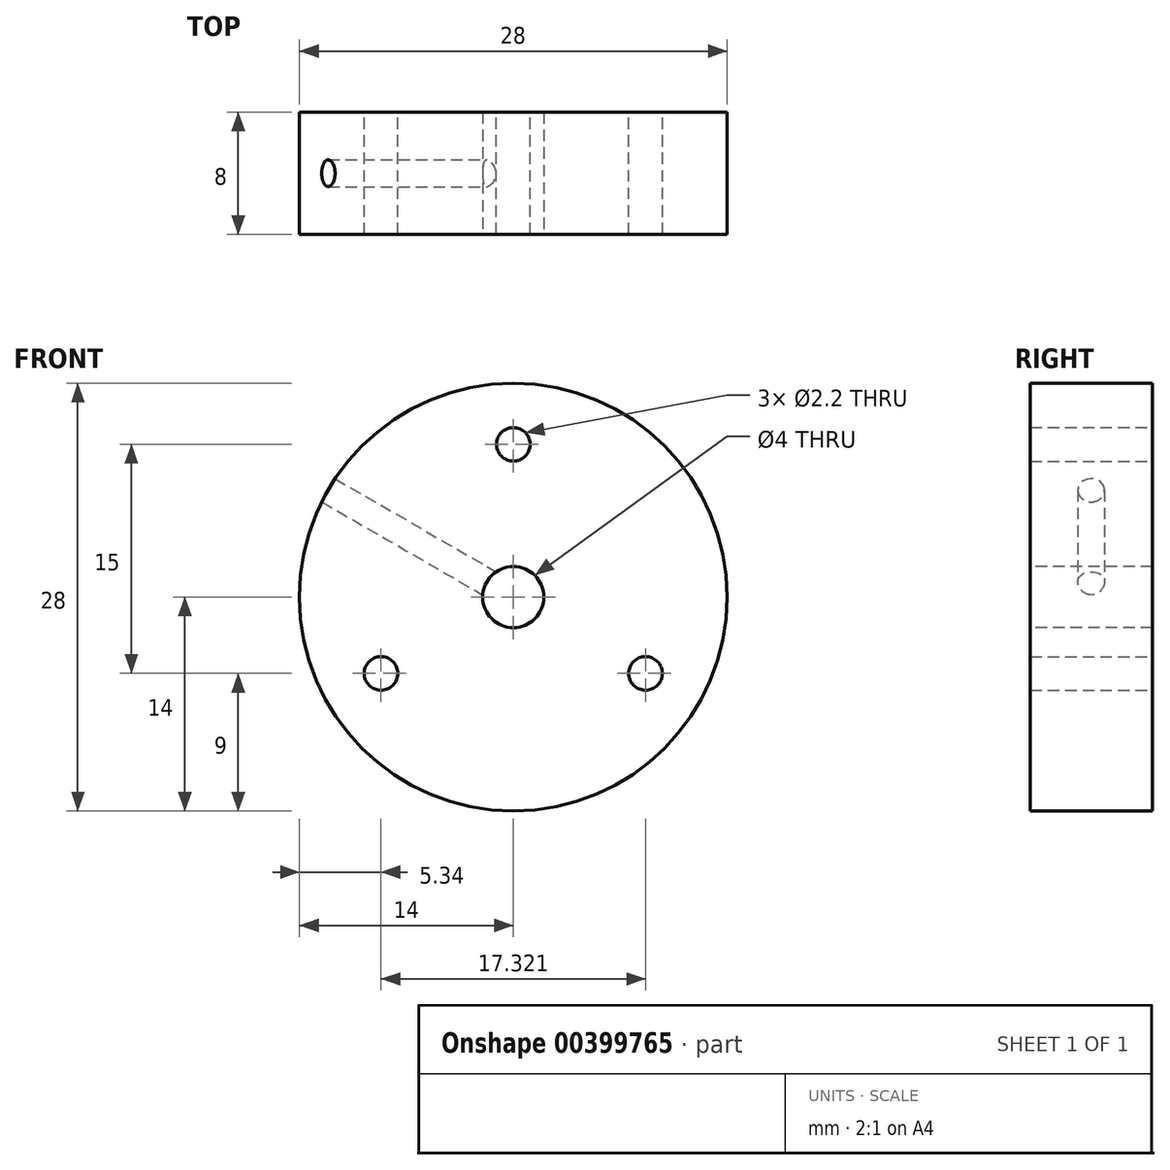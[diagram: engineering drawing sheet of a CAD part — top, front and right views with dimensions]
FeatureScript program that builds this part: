
annotation { "Feature Type Name" : "Feature", "Feature Type Description" : "" }
export const myFeature = defineFeature(function(context is Context, id is Id, definition is map)
    precondition{}
    {
        {
            var Q0;
            Q0=qCreatedBy(makeId("Front.planeOp"),FACE);
            var sketch = newSketch(context, id + "F0", { "sketchPlane" : qUnion([Q0])});
            skCircle(sketch, "E0", {"center": v(0, 0) * mm, "radius": 10 * mm, "construction": true});
            skLineSegment(sketch, "E1.0", {"start": v(0, 10) * mm, "end": v(8.66, -5) * mm, "construction": true});
            skLineSegment(sketch, "E1.1", {"start": v(8.66, -5) * mm, "end": v(-8.66, -5) * mm, "construction": true});
            skLineSegment(sketch, "E1.2", {"start": v(-8.66, -5) * mm, "end": v(0, 10) * mm, "construction": true});
            skCircle(sketch, "E2", {"center": v(0, 10) * mm, "radius": 1.1 * mm});
            skCircle(sketch, "E3", {"center": v(8.66, -5) * mm, "radius": 1.1 * mm});
            skCircle(sketch, "E4", {"center": v(-8.66, -5) * mm, "radius": 1.1 * mm});
            skCircle(sketch, "E5", {"center": v(0, 0) * mm, "radius": 14 * mm});
            skSolve(sketch);
        }
        {
            var Q0;
            Q0=makeQuery(id+"F0.imprint","IMPRINT",FACE,{"disambiguationData":[TD([[makeQuery(id+"F0.imprint","IMPRINT",EDGE,{"derivedFrom":sQuery(id+"F0.wireOp",EDGE,"E2")}),-1.0]])]});
            extrude(context, id + "F1", {"entities" : qUnion([Q0]), "depth" : 8 * mm});
        }
        {
            var Q0;
            Q0=makeQuery(id+"F1.opExtrude","CAP_FACE",FACE,{"disambiguationData":[OSD([sQuery(id+"F0.wireOp",EDGE,"E2"),sQuery(id+"F0.wireOp",EDGE,"E3"),sQuery(id+"F0.wireOp",EDGE,"E4"),sQuery(id+"F0.wireOp",EDGE,"E5")])],"isStart":false});
            var sketch = newSketch(context, id + "F2", { "sketchPlane" : qUnion([Q0])});
            skCircle(sketch, "E6", {"center": v(0, 0) * mm, "radius": 2 * mm});
            skSolve(sketch);
        }
        {
            var Q0;
            Q0 = qSketchRegion(id + "F2", true);
            extrude(context, id + "F3", {"entities" : qUnion([Q0]), "operationType" : NewBodyOperationType.REMOVE, "endBound" : BoundingType.THROUGH_ALL, "oppositeDirection" : true, "depth" : 25 * mm});
        }
        {
            var Q0;
            Q0=qCreatedBy(makeId("Right.planeOp"),FACE);
            var sketch = newSketch(context, id + "F4", { "sketchPlane" : qUnion([Q0])});
            skLineSegment(sketch, "E7", {"start": v(32.06, 0) * mm, "end": v(-30.06, 0) * mm, "construction": true});
            skSolve(sketch);
        }
        {
            var Q0;
            Q0=sQuery(id+"F4.wireOp",EDGE,"E7");
            cPlane(context, id + "F5", {"entities" : qUnion([Q0]), "cplaneType" : CPlaneType.LINE_ANGLE, "offset" : 25 * mm, "angle" : 60 * degree, "width" : 150 * mm, "height" : 150 * mm});
        }
        {
            var Q0;
            Q0=qCreatedBy(id+"F5.planeOp",FACE);
            var sketch = newSketch(context, id + "F6", { "sketchPlane" : qUnion([Q0])});
            skCircle(sketch, "E8", {"center": v(-4, 0) * mm, "radius": 0.88 * mm});
            skSolve(sketch);
        }
        {
            var Q0;
            Q0 = qSketchRegion(id + "F6", true);
            extrude(context, id + "F7", {"entities" : qUnion([Q0]), "operationType" : NewBodyOperationType.REMOVE, "endBound" : BoundingType.THROUGH_ALL, "oppositeDirection" : true, "depth" : 25 * mm});
        }
    });
